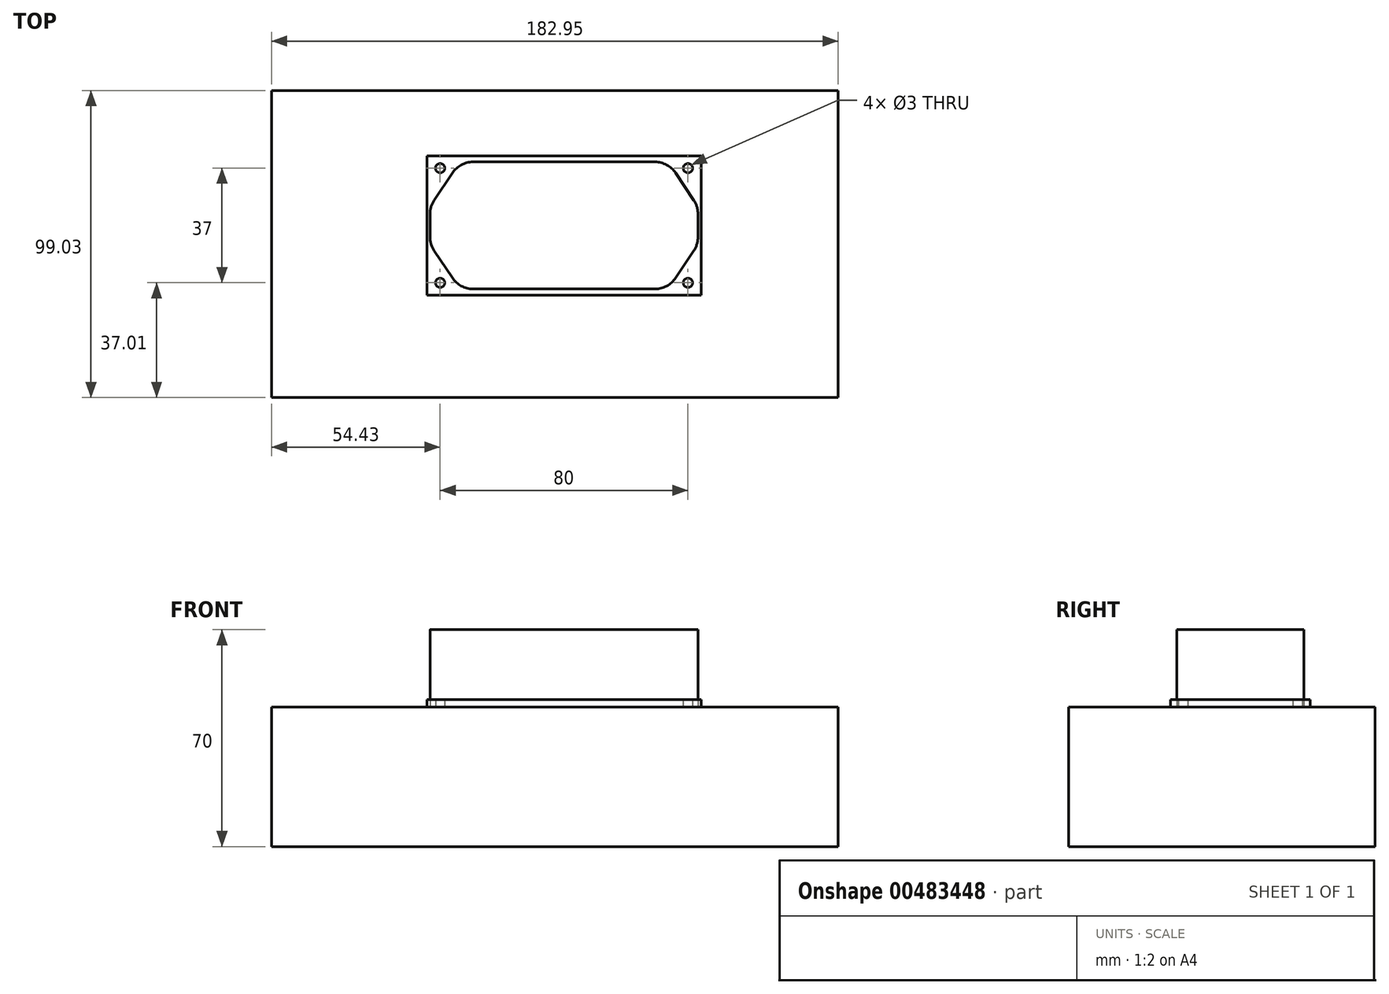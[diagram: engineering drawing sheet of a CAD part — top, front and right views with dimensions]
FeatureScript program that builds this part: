
annotation { "Feature Type Name" : "Feature", "Feature Type Description" : "" }
export const myFeature = defineFeature(function(context is Context, id is Id, definition is map)
    precondition{}
    {
        {
            var Q0;
            Q0=qCreatedBy(makeId("Top.planeOp"),FACE);
            var sketch = newSketch(context, id + "F0", { "sketchPlane" : qUnion([Q0])});
            skLineSegment(sketch, "E0.bottom", {"start": v(-94.43, 43.52) * mm, "end": v(88.52, 43.52) * mm});
            skLineSegment(sketch, "E0.top", {"start": v(-94.43, -55.51) * mm, "end": v(88.52, -55.51) * mm});
            skLineSegment(sketch, "E0.left", {"start": v(-94.43, 43.52) * mm, "end": v(-94.43, -55.51) * mm});
            skLineSegment(sketch, "E0.right", {"start": v(88.52, 43.52) * mm, "end": v(88.52, -55.51) * mm});
            skSolve(sketch);
        }
        {
            var Q0;
            Q0 = qSketchRegion(id + "F0", true);
            extrude(context, id + "F1", {"entities" : qUnion([Q0]), "oppositeDirection" : true, "depth" : 45 * mm});
        }
        {
            var Q0;
            Q0=qCreatedBy(makeId("Top.planeOp"),FACE);
            var sketch = newSketch(context, id + "F2", { "sketchPlane" : qUnion([Q0])});
            skLineSegment(sketch, "E1", {"start": v(-31, 19.5) * mm, "end": v(31, 19.5) * mm});
            skLineSegment(sketch, "E2", {"start": v(34, 16.5) * mm, "end": v(34, 6.5) * mm});
            skLineSegment(sketch, "E3", {"start": v(34, 6.5) * mm, "end": v(39.75, 6.5) * mm});
            skLineSegment(sketch, "E4", {"start": v(42.75, 3.5) * mm, "end": v(42.75, -3.5) * mm});
            skLineSegment(sketch, "E5", {"start": v(39.75, -6.5) * mm, "end": v(34, -6.5) * mm});
            skLineSegment(sketch, "E6", {"start": v(34, -6.5) * mm, "end": v(34, -16.5) * mm});
            skLineSegment(sketch, "E7", {"start": v(31, -19.5) * mm, "end": v(-31, -19.5) * mm});
            skLineSegment(sketch, "E8", {"start": v(-34, -16.5) * mm, "end": v(-34, -6.5) * mm});
            skLineSegment(sketch, "E9", {"start": v(-34, -6.5) * mm, "end": v(-39.75, -6.5) * mm});
            skLineSegment(sketch, "E10", {"start": v(-42.75, -3.5) * mm, "end": v(-42.75, 3.5) * mm});
            skLineSegment(sketch, "E11", {"start": v(-39.75, 6.5) * mm, "end": v(-34, 6.5) * mm});
            skLineSegment(sketch, "E12", {"start": v(-34, 6.5) * mm, "end": v(-34, 16.5) * mm});
            skPoint(sketch, "E13.visualSharp", {"position": v(-34, 19.5) * mm});
            skArc(sketch, "E13.filletArc", {"start": v(-31, 19.5) * mm, "mid": v(-33.12, 18.62) * mm, "end": v(-34, 16.5) * mm});
            skPoint(sketch, "E14.visualSharp", {"position": v(34, 19.5) * mm});
            skArc(sketch, "E14.filletArc", {"start": v(34, 16.5) * mm, "mid": v(33.12, 18.62) * mm, "end": v(31, 19.5) * mm});
            skPoint(sketch, "E15.visualSharp", {"position": v(42.75, 6.5) * mm});
            skArc(sketch, "E15.filletArc", {"start": v(42.75, 3.5) * mm, "mid": v(41.87, 5.62) * mm, "end": v(39.75, 6.5) * mm});
            skPoint(sketch, "E16.visualSharp", {"position": v(42.75, -6.5) * mm});
            skArc(sketch, "E16.filletArc", {"start": v(39.75, -6.5) * mm, "mid": v(41.87, -5.62) * mm, "end": v(42.75, -3.5) * mm});
            skPoint(sketch, "E17.visualSharp", {"position": v(34, -19.5) * mm});
            skArc(sketch, "E17.filletArc", {"start": v(31, -19.5) * mm, "mid": v(33.12, -18.62) * mm, "end": v(34, -16.5) * mm});
            skPoint(sketch, "E18.visualSharp", {"position": v(-34, -19.5) * mm});
            skArc(sketch, "E18.filletArc", {"start": v(-34, -16.5) * mm, "mid": v(-33.12, -18.62) * mm, "end": v(-31, -19.5) * mm});
            skPoint(sketch, "E19.visualSharp", {"position": v(-42.75, -6.5) * mm});
            skArc(sketch, "E19.filletArc", {"start": v(-42.75, -3.5) * mm, "mid": v(-41.87, -5.62) * mm, "end": v(-39.75, -6.5) * mm});
            skPoint(sketch, "E20.visualSharp", {"position": v(-42.75, 6.5) * mm});
            skArc(sketch, "E20.filletArc", {"start": v(-39.75, 6.5) * mm, "mid": v(-41.87, 5.62) * mm, "end": v(-42.75, 3.5) * mm});
            skSolve(sketch);
        }
        {
            var Q0;
            Q0=qCreatedBy(makeId("Top.planeOp"),FACE);
            var sketch = newSketch(context, id + "F3", { "sketchPlane" : qUnion([Q0])});
            skLineSegment(sketch, "E21", {"start": v(-29.39, 20.5) * mm, "end": v(29.39, 20.5) * mm});
            skLineSegment(sketch, "E22", {"start": v(36.04, 16.94) * mm, "end": v(41.9, 8.15) * mm});
            skLineSegment(sketch, "E23", {"start": v(43.25, 3.71) * mm, "end": v(43.25, -3.71) * mm});
            skLineSegment(sketch, "E24", {"start": v(41.9, -8.15) * mm, "end": v(36.04, -16.94) * mm});
            skLineSegment(sketch, "E25", {"start": v(29.39, -20.5) * mm, "end": v(-29.39, -20.5) * mm});
            skLineSegment(sketch, "E26", {"start": v(-36.04, -16.94) * mm, "end": v(-41.9, -8.15) * mm});
            skLineSegment(sketch, "E27", {"start": v(-43.25, -3.71) * mm, "end": v(-43.25, 3.71) * mm});
            skLineSegment(sketch, "E28", {"start": v(-41.9, 8.15) * mm, "end": v(-36.04, 16.94) * mm});
            skPoint(sketch, "E29.visualSharp", {"position": v(-33.67, 20.5) * mm});
            skArc(sketch, "E29.filletArc", {"start": v(-29.39, 20.5) * mm, "mid": v(-33.16, 19.55) * mm, "end": v(-36.04, 16.94) * mm});
            skPoint(sketch, "E30.visualSharp", {"position": v(33.67, 20.5) * mm});
            skArc(sketch, "E30.filletArc", {"start": v(36.04, 16.94) * mm, "mid": v(33.16, 19.55) * mm, "end": v(29.39, 20.5) * mm});
            skPoint(sketch, "E31.visualSharp", {"position": v(43.25, 6.14) * mm});
            skArc(sketch, "E31.filletArc", {"start": v(43.25, 3.71) * mm, "mid": v(42.9, 6.03) * mm, "end": v(41.9, 8.15) * mm});
            skPoint(sketch, "E32.visualSharp", {"position": v(43.25, -6.14) * mm});
            skArc(sketch, "E32.filletArc", {"start": v(41.9, -8.15) * mm, "mid": v(42.9, -6.03) * mm, "end": v(43.25, -3.71) * mm});
            skPoint(sketch, "E33.visualSharp", {"position": v(33.67, -20.5) * mm});
            skArc(sketch, "E33.filletArc", {"start": v(29.39, -20.5) * mm, "mid": v(33.16, -19.55) * mm, "end": v(36.04, -16.94) * mm});
            skPoint(sketch, "E34.visualSharp", {"position": v(-33.67, -20.5) * mm});
            skArc(sketch, "E34.filletArc", {"start": v(-36.04, -16.94) * mm, "mid": v(-33.16, -19.55) * mm, "end": v(-29.39, -20.5) * mm});
            skPoint(sketch, "E35.visualSharp", {"position": v(-43.25, -6.14) * mm});
            skArc(sketch, "E35.filletArc", {"start": v(-43.25, -3.71) * mm, "mid": v(-42.9, -6.03) * mm, "end": v(-41.9, -8.15) * mm});
            skPoint(sketch, "E36.visualSharp", {"position": v(-43.25, 6.14) * mm});
            skArc(sketch, "E36.filletArc", {"start": v(-41.9, 8.15) * mm, "mid": v(-42.9, 6.03) * mm, "end": v(-43.25, 3.71) * mm});
            skSolve(sketch);
        }
        {
            var Q0;
            Q0=qCreatedBy(makeId("Top.planeOp"),FACE);
            var sketch = newSketch(context, id + "F4", { "sketchPlane" : qUnion([Q0])});
            skLineSegment(sketch, "E37.bottom", {"start": v(-44.25, 22.5) * mm, "end": v(44.25, 22.5) * mm});
            skLineSegment(sketch, "E37.top", {"start": v(-44.25, -22.5) * mm, "end": v(44.25, -22.5) * mm});
            skLineSegment(sketch, "E37.left", {"start": v(-44.25, 22.5) * mm, "end": v(-44.25, -22.5) * mm});
            skLineSegment(sketch, "E37.right", {"start": v(44.25, 22.5) * mm, "end": v(44.25, -22.5) * mm});
            skCircle(sketch, "E38", {"center": v(-40, 18.5) * mm, "radius": 1.5 * mm});
            skCircle(sketch, "E39", {"center": v(40, 18.5) * mm, "radius": 1.5 * mm});
            skCircle(sketch, "E40", {"center": v(40, -18.5) * mm, "radius": 1.5 * mm});
            skCircle(sketch, "E41", {"center": v(-40, -18.5) * mm, "radius": 1.5 * mm});
            skSolve(sketch);
        }
        {
            var Q0;
            Q0 = qSketchRegion(id + "F4", true);
            extrude(context, id + "F5", {"entities" : qUnion([Q0]), "depth" : 2.5 * mm});
        }
        {
            var Q0;
            Q0 = qSketchRegion(id + "F3", true);
            extrude(context, id + "F6", {"entities" : qUnion([Q0]), "depth" : 25 * mm, "offsetDistance" : 25 * mm});
        }
    });
